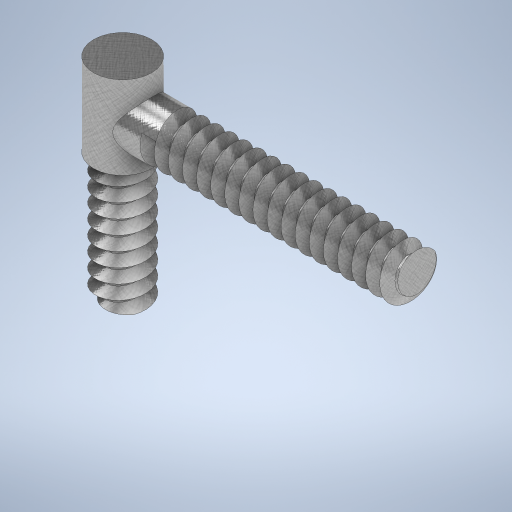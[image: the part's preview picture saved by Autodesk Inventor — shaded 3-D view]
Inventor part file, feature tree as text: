
AUTODESK INVENTOR PART (.ipt)
format: ipt  version: 2024 (Build 280153020, 153B)  size: 670,208 bytes
history: native  units: mm
features: sketch x5, extrude x3, helix x2, plane x2
ambient origin geometry x8: Origin, YZ Plane, XZ Plane, XY Plane, X Axis, Y Axis, Z Axis, Center Point
bodies: Solid1 (feature_tree)
feature tree (12):
  extrude  "Extrusion1"  Depth=1.7mm TaperAngle=0.0deg
  helix  "Coil1"  [1 undecoded]
  extrude  "Extrusion2"  Depth=0.2mm
  plane  "Work Plane1"
  extrude  "Extrusion4"  Depth=1.7mm
  plane  "Work Plane2"
  helix  "Coil3"  [1 undecoded]
  sketch  "Sketch1"  dims[d0=6.0mm d1=20.0mm d2=0.0mm d3=1.7mm]
  sketch  "Sketch2"  dims[d4=60.0deg d5=0.2mm]
  sketch  "Sketch4"  dims[d6=2.0mm]
  sketch  "Sketch8"  dims[d7=1.7mm d8=22.0mm d9=10.0mm d10=0.0mm d11=90.0deg d12=90.0deg d13=0.0mm d14=0.0mm d15=6.0mm d16=35.0mm d17=0.0mm]
  sketch  "Sketch9"  dims[d28=23.0mm d42=7.0mm d43=10.0mm d44=0.0mm d45=0.0mm d46=1.7mm d47=60.0deg d48=0.2mm d49=2.0mm d50=1.7mm d51=32.0mm d52=10.0mm d53=0.0mm d54=90.0deg d55=90.0deg d56=0.0mm d57=0.0mm]
note: 2 required parameter values undecoded (feature->parameter linkage not recoverable at this tier; creation-order binding heuristic only, values carry confidence <= 0.55)
